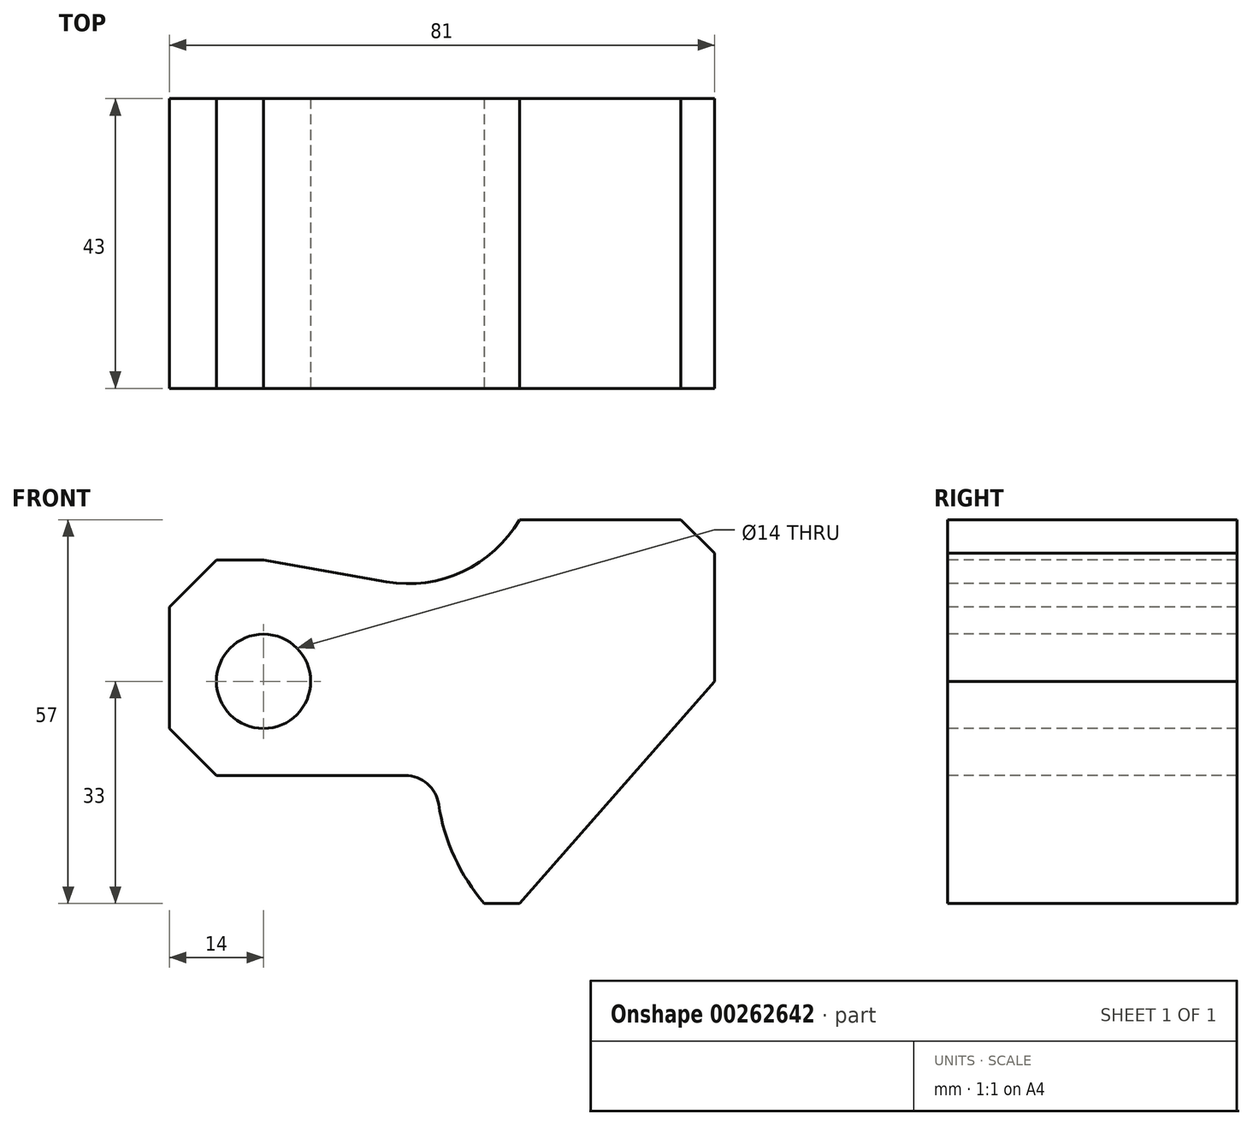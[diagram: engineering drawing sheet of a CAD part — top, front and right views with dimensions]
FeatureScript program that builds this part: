
annotation { "Feature Type Name" : "Feature", "Feature Type Description" : "" }
export const myFeature = defineFeature(function(context is Context, id is Id, definition is map)
    precondition{}
    {
        {
            var Q0;
            Q0=qCreatedBy(makeId("Front.planeOp"),FACE);
            var sketch = newSketch(context, id + "F0", { "sketchPlane" : qUnion([Q0])});
            skLineSegment(sketch, "E0.bottom", {"start": v(40.5, 28.5) * mm, "end": v(-40.5, 28.5) * mm});
            skLineSegment(sketch, "E0.top", {"start": v(40.5, -28.5) * mm, "end": v(-40.5, -28.5) * mm});
            skLineSegment(sketch, "E0.left", {"start": v(40.5, 28.5) * mm, "end": v(40.5, -28.5) * mm});
            skLineSegment(sketch, "E0.right", {"start": v(-40.5, 28.5) * mm, "end": v(-40.5, -28.5) * mm});
            skPoint(sketch, "E0.middle", {"position": v(0, 0) * mm});
            skPoint(sketch, "E1", {"position": v(40.5, 4.5) * mm});
            skPoint(sketch, "E2", {"position": v(40.5, 23.5) * mm});
            skLineSegment(sketch, "E3", {"start": v(40.5, 4.5) * mm, "end": v(11.5, -28.5) * mm});
            skCircle(sketch, "E4", {"center": v(-26.5, 4.5) * mm, "radius": 7 * mm});
            skLineSegment(sketch, "E5", {"start": v(40.5, 23.5) * mm, "end": v(35.5, 28.5) * mm});
            skPoint(sketch, "E6", {"position": v(-40.5, 4.5) * mm});
            skPoint(sketch, "E7", {"position": v(-40.5, -2.5) * mm});
            skPoint(sketch, "E8", {"position": v(-40.5, -9.5) * mm});
            skLineSegment(sketch, "E9", {"start": v(-40.5, -9.5) * mm, "end": v(-5.43, -9.5) * mm});
            skLineSegment(sketch, "E10", {"start": v(-40.5, -2.5) * mm, "end": v(-33.5, -9.5) * mm});
            skPoint(sketch, "E11", {"position": v(-40.5, 22.5) * mm});
            skLineSegment(sketch, "E12", {"start": v(-40.5, 22.5) * mm, "end": v(-26.5, 22.5) * mm});
            skPoint(sketch, "E13", {"position": v(-40.5, 15.5) * mm});
            skLineSegment(sketch, "E14", {"start": v(-40.5, 15.5) * mm, "end": v(-33.5, 22.5) * mm});
            skPoint(sketch, "E15", {"position": v(11.5, 28.5) * mm});
            skPoint(sketch, "E16", {"position": v(28.2, -9.5) * mm});
            skArc(sketch, "E17", {"start": v(-0.49, -13.76) * mm, "mid": v(-2.17, -10.71) * mm, "end": v(-5.43, -9.5) * mm});
            skArc(sketch, "E18", {"start": v(-0.49, -13.76) * mm, "mid": v(1.85, -21.62) * mm, "end": v(6.29, -28.5) * mm});
            skLineSegment(sketch, "E19", {"start": v(-26.5, 22.5) * mm, "end": v(-8.26, 19.28) * mm});
            skArc(sketch, "E20", {"start": v(-8.26, 19.28) * mm, "mid": v(3.07, 20.78) * mm, "end": v(11.5, 28.5) * mm});
            skSolve(sketch);
        }
        {
            var Q0;
            {var subQ5=sQuery(id+"F0.wireOp",EDGE,"E3");Q0=makeQuery(id+"F0.imprint","IMPRINT",FACE,{"disambiguationData":[TD([[makeQuery(id+"F0.imprint","IMPRINT",EDGE,{"derivedFrom":subQ5}),-1.0]])]});}
            extrude(context, id + "F1", {"entities" : qUnion([Q0]), "oppositeDirection" : true, "depth" : 43 * mm});
        }
    });
